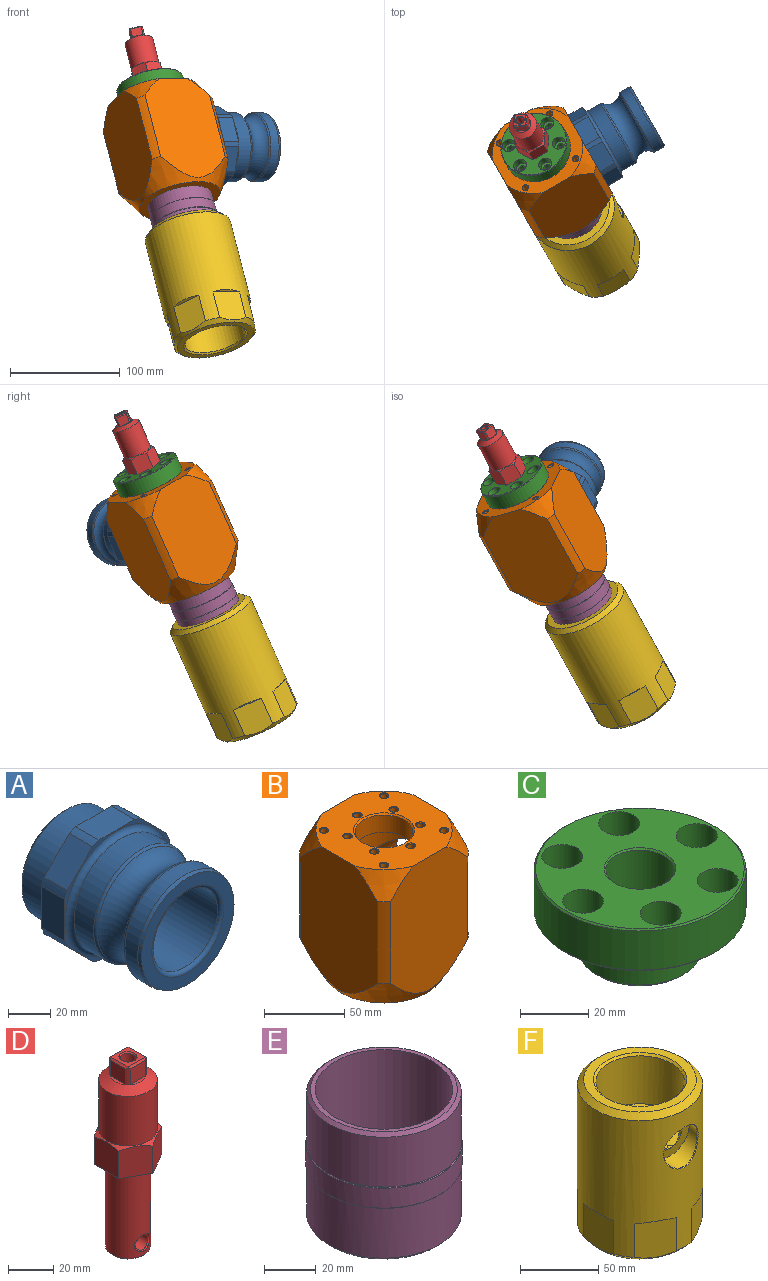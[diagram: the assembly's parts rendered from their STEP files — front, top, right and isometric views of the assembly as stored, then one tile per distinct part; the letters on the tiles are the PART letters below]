
ASSEMBLY  parts=6 mates=14
PART A: 42 faces, bbox 80.5x83x80.5 mm
  f0: plane 70x70mm, normal (0,-1,0), area 304.1mm2, adj f1,f2,f4,f5,f6,f7,f8,f9
  f1: cylinder r=37mm len=15.5mm, axis (0,-1,0), area 71.6mm2, adj f0,f3,f36,f37
  f2: cylinder r=37mm len=15.5mm, axis (0,-1,0), area 71.6mm2, adj f0,f3,f35,f37
  f3: plane 70x70mm, normal (0,1,0), area 622.2mm2, adj f1,f2,f4,f5,f6,f7,f8,f9
  f4: cylinder r=37mm len=15.5mm, axis (0,-1,0), area 71.6mm2, adj f0,f3,f30,f36
  f5: cylinder r=37mm len=15.5mm, axis (0,-1,0), area 71.6mm2, adj f0,f3,f34,f35
  f6: cylinder r=37mm len=15.5mm, axis (0,-1,0), area 71.6mm2, adj f0,f3,f33,f34
  f7: cylinder r=37mm len=15.5mm, axis (0,-1,0), area 71.6mm2, adj f0,f3,f32,f33
  f8: cylinder r=37mm len=15.5mm, axis (0,-1,0), area 71.6mm2, adj f0,f3,f31,f32
  f9: cylinder r=37mm len=15.5mm, axis (0,-1,0), area 71.6mm2, adj f0,f3,f30,f31
  f10: torus R=24mm, axis (0,-1,0), area 448.6mm2, adj f11,f29
  f11: plane 61.93x61.93mm, normal (0,-1,0), area 1202.5mm2, adj f10,f12
  f12: cone r=31.5mm half-angle=15deg, axis (0,1,0), area 406.3mm2, adj f11,f13
  f13: cylinder r=31.5mm len=63mm, axis (0,-1,0), area 1687.4mm2, adj f12,f14
  f14: torus R=29.5mm, axis (0,-1,0), area 367.6mm2, adj f13,f15
  f15: torus R=37.2mm, axis (0,-1,0), area 3592.5mm2, adj f14,f16
  f16: torus R=29.5mm, axis (0,-1,0), area 367.6mm2, adj f15,f17
  f17: cylinder r=31.5mm len=63mm, axis (0,-1,0), area 2578.1mm2, adj f16,f18
  f18: torus R=34.5mm, axis (0,-1,0), area 965mm2, adj f0,f17
  f19: cylinder r=33mm len=66mm, axis (0,-1,0), area 311mm2, adj f3,f41
  f20: plane 65x65mm, normal (0,1,0), area 395.8mm2, adj f40,f41
  f21: cylinder r=30mm len=60mm, axis (0,-1,0), area 282.7mm2, adj f22,f40
  f22: plane 60x60mm, normal (0,1,0), area 230.7mm2, adj f21,f38
  f23: cylinder r=28.25mm len=56.5mm, axis (0,-1,0), area 443.7mm2, adj f38,f39
  f24: plane 60x60mm, normal (0,-1,0), area 230.7mm2, adj f25,f39
  f25: cylinder r=30mm len=60mm, axis (0,-1,0), area 2733.2mm2, adj f24,f26
  f26: cone r=28mm half-angle=45deg, axis (0,-1,0), area 515.4mm2, adj f25,f27
  f27: plane 56x56mm, normal (0,1,0), area 653.5mm2, adj f26,f28
  f28: torus R=24mm, axis (0,-1,0), area 448.6mm2, adj f27,f29
  f29: cylinder r=22mm len=79mm, axis (0,-1,0), area 10920.2mm2, adj f10,f28
  f30: plane 16.97x16.97mm, normal (-0.71,0,0.71), area 372mm2, adj f0,f3,f4,f9
  f31: plane 24x15.5mm, normal (-1,0,0), area 372mm2, adj f0,f3,f8,f9
  f32: plane 16.97x16.97mm, normal (-0.71,0,-0.71), area 372mm2, adj f0,f3,f7,f8
  f33: plane 24x15.5mm, normal (0,0,-1), area 372mm2, adj f0,f3,f6,f7
  f34: plane 16.97x16.97mm, normal (0.71,0,-0.71), area 372mm2, adj f0,f3,f5,f6
  f35: plane 24x15.5mm, normal (1,0,0), area 372mm2, adj f0,f2,f3,f5
  f36: plane 24x15.5mm, normal (0,0,1), area 372mm2, adj f0,f1,f3,f4
  f37: plane 16.97x16.97mm, normal (0.71,0,0.71), area 372mm2, adj f0,f1,f2,f3
  f38: torus R=28.75mm, axis (0,-1,0), area 140.3mm2, adj f22,f23
  f39: torus R=28.75mm, axis (0,1,0), area 140.3mm2, adj f23,f24
  f40: torus R=30.5mm, axis (0,-1,0), area 148.9mm2, adj f20,f21
  f41: torus R=32.5mm, axis (0,-1,0), area 162mm2, adj f19,f20
PART B: 56 faces, bbox 105x105x105 mm
  f0: cylinder r=26mm len=63mm, axis (0,0,-1), area 6906.9mm2, adj f18,f19,f39,f40,f41
  f1: plane 80x80mm, normal (0,0,1), area 4065mm2, adj f4,f6,f8,f10,f11,f12,f13,f14
  f2: plane 76x76mm, normal (0,0,-1), area 1741.4mm2, adj f15,f46
  f3: cylinder r=52.5mm len=62.56mm, axis (0,0,-1), area 531.1mm2, adj f4,f10,f11,f15
  f4: plane 101.56x68.04mm, normal (1,0,0), area 3286.4mm2, adj f1,f3,f5,f11,f12,f15,f45
  f5: cylinder r=52.5mm len=62.56mm, axis (0,0,-1), area 531.1mm2, adj f4,f6,f12,f15
  f6: plane 101.56x68.04mm, normal (0,1,0), area 6081.5mm2, adj f1,f5,f7,f12,f13,f15
  f7: cylinder r=52.5mm len=62.56mm, axis (0,0,-1), area 531.1mm2, adj f6,f8,f13,f15
  f8: plane 101.56x68.04mm, normal (-1,0,0), area 6081.5mm2, adj f1,f7,f9,f13,f14,f15
  f9: cylinder r=52.5mm len=62.56mm, axis (0,0,-1), area 531.1mm2, adj f8,f10,f14,f15
  f10: plane 101.56x68.04mm, normal (0,-1,0), area 6081.5mm2, adj f1,f3,f9,f11,f14,f15
  f11: cone r=42.5mm half-angle=30deg, axis (0,0,-1), area 425.1mm2, adj f1,f3,f4,f10
  f12: cone r=42.5mm half-angle=30deg, axis (0,0,-1), area 425.1mm2, adj f1,f4,f5,f6
  f13: cone r=42.5mm half-angle=30deg, axis (0,0,-1), area 425.1mm2, adj f1,f6,f7,f8
  f14: cone r=42.5mm half-angle=30deg, axis (0,0,-1), area 425.1mm2, adj f1,f8,f9,f10
  f15: cone r=55mm half-angle=30deg, axis (0,0,1), area 3590.8mm2, adj f2,f3,f4,f5,f6,f7,f8,f9
  f16: cone r=19mm half-angle=45deg, axis (0,0,1), area 164.4mm2, adj f1,f17
  f17: cylinder r=18mm len=36mm, axis (0,0,-1), area 1492.1mm2, adj f16,f18
  f18: cone r=18mm half-angle=59deg, axis (0,0,-1), area 1290.1mm2, adj f0,f17
  f19: plane 56.66x56.66mm, normal (0,0,-1), area 397.3mm2, adj f0,f20
  f20: cylinder r=28.33mm len=56.66mm, axis (0,0,-1), area 3826.8mm2, adj f19,f46
  f21: cone r=3mm half-angle=46deg, axis (0,0,1), area 12mm2, adj f1,f22
  f22: cylinder r=2.5mm len=14.52mm, axis (0,0,1), area 228mm2, adj f21,f23
  f23: cone r=2.5mm half-angle=59deg, axis (0,0,1), area 22.9mm2, adj f22
  f24: cone r=3mm half-angle=46deg, axis (0,0,1), area 12mm2, adj f1,f25
  f25: cylinder r=2.5mm len=14.52mm, axis (0,0,1), area 228mm2, adj f24,f26
  f26: cone r=2.5mm half-angle=59deg, axis (0,0,1), area 22.9mm2, adj f25
  f27: cone r=3mm half-angle=46deg, axis (0,0,1), area 12mm2, adj f1,f28
  f28: cylinder r=2.5mm len=14.52mm, axis (0,0,1), area 228mm2, adj f27,f29
  f29: cone r=2.5mm half-angle=59deg, axis (0,0,1), area 22.9mm2, adj f28
  f30: cone r=3mm half-angle=46deg, axis (0,0,1), area 12mm2, adj f1,f31
  f31: cylinder r=2.5mm len=14.52mm, axis (0,0,1), area 228mm2, adj f30,f32
  f32: cone r=2.5mm half-angle=59deg, axis (0,0,1), area 22.9mm2, adj f31
  f33: cone r=3mm half-angle=46deg, axis (0,0,1), area 12mm2, adj f1,f34
  f34: cylinder r=2.5mm len=14.52mm, axis (0,0,1), area 228mm2, adj f33,f35
  f35: cone r=2.5mm half-angle=59deg, axis (0,0,1), area 22.9mm2, adj f34
  f36: cone r=3mm half-angle=46deg, axis (0,0,1), area 12mm2, adj f1,f37
  f37: cylinder r=2.5mm len=14.52mm, axis (0,0,1), area 228mm2, adj f36,f38
  f38: cone r=2.5mm half-angle=59deg, axis (0,0,1), area 22.9mm2, adj f37
  f39: plane 22.49x2.33mm, normal (1,0,0), area 35.2mm2, adj f0,f40
  f40: cylinder r=28.33mm len=56.66mm, axis (1,0,0), area 4362.6mm2, adj f0,f39,f41,f45
  f41: plane 22.49x2.33mm, normal (1,0,0), area 35.2mm2, adj f0,f40
  f42: cone r=3mm half-angle=46deg, axis (0,0,1), area 12mm2, adj f1,f43
  f43: cylinder r=2.5mm len=14.52mm, axis (0,0,1), area 228mm2, adj f42,f44
  f44: cone r=2.5mm half-angle=59deg, axis (0,0,1), area 22.9mm2, adj f43
  f45: cone r=28.33mm half-angle=45deg, axis (1,0,0), area 387.6mm2, adj f4,f40
  f46: cone r=28.33mm half-angle=45deg, axis (0,0,-1), area 387.6mm2, adj f2,f20
  f47: cone r=3mm half-angle=46deg, axis (0,0,1), area 12mm2, adj f1,f48
  f48: cylinder r=2.5mm len=14.52mm, axis (0,0,1), area 228mm2, adj f47,f49
  f49: cone r=2.5mm half-angle=59deg, axis (0,0,1), area 22.9mm2, adj f48
  f50: cone r=3mm half-angle=46deg, axis (0,0,1), area 12mm2, adj f1,f51
  f51: cylinder r=2.5mm len=14.52mm, axis (0,0,1), area 228mm2, adj f50,f52
  f52: cone r=2.5mm half-angle=59deg, axis (0,0,1), area 22.9mm2, adj f51
  f53: cone r=3mm half-angle=46deg, axis (0,0,1), area 12mm2, adj f1,f54
  f54: cylinder r=2.5mm len=14.52mm, axis (0,0,1), area 228mm2, adj f53,f55
  f55: cone r=2.5mm half-angle=59deg, axis (0,0,1), area 22.9mm2, adj f54
PART C: 37 faces, bbox 62x62x30 mm
  f0: cylinder r=17.98mm len=35.95mm, axis (0,0,-1), area 609.9mm2, adj f1,f18
  f1: plane 35.95x35.95mm, normal (0,0,-1), area 159.8mm2, adj f0,f2
  f2: cylinder r=16.5mm len=33mm, axis (0,0,-1), area 269.5mm2, adj f1,f3
  f3: plane 35.95x35.95mm, normal (0,0,1), area 159.8mm2, adj f2,f4
  f4: cylinder r=17.98mm len=35.95mm, axis (0,0,-1), area 677.6mm2, adj f3,f5
  f5: cone r=16.98mm half-angle=45deg, axis (0,0,1), area 155.3mm2, adj f4,f6
  f6: plane 33.95x33.95mm, normal (0,0,-1), area 558.9mm2, adj f5,f7
  f7: cone r=10mm half-angle=45deg, axis (0,0,-1), area 45.5mm2, adj f6,f8
  f8: cylinder r=10mm len=20mm, axis (0,0,-1), area 157.1mm2, adj f7,f9
  f9: plane 23x23mm, normal (0,0,1), area 101.3mm2, adj f8,f10
  f10: cylinder r=11.5mm len=23mm, axis (0,0,-1), area 187.9mm2, adj f9,f11
  f11: plane 23x23mm, normal (0,0,-1), area 101.3mm2, adj f10,f12
  f12: cylinder r=10mm len=23.9mm, axis (0,0,-1), area 1501.7mm2, adj f11,f13
  f13: cone r=10.5mm half-angle=45deg, axis (0,0,1), area 45.5mm2, adj f12,f14
  f14: plane 61x61mm, normal (0,0,1), area 1897.5mm2, adj f13,f15,f19,f22,f25,f28,f31,f34
  f15: cone r=31mm half-angle=45deg, axis (0,0,-1), area 136.6mm2, adj f14,f16
  f16: cylinder r=31mm len=62mm, axis (0,0,-1), area 2726.9mm2, adj f15,f17
  f17: cone r=30.5mm half-angle=45deg, axis (0,0,1), area 136.6mm2, adj f16,f18
  f18: plane 61x61mm, normal (0,0,-1), area 1676.5mm2, adj f0,f17,f21,f24,f27,f30,f33,f36
  f19: cylinder r=6mm len=12mm, axis (0,0,1), area 339.3mm2, adj f14,f20
  f20: plane 12x12mm, normal (0,0,1), area 74.6mm2, adj f19,f21
  f21: cylinder r=3.5mm len=7mm, axis (0,0,1), area 131.9mm2, adj f18,f20
  f22: cylinder r=6mm len=12mm, axis (0,0,1), area 339.3mm2, adj f14,f23
  f23: plane 12x12mm, normal (0,0,1), area 74.6mm2, adj f22,f24
  f24: cylinder r=3.5mm len=7mm, axis (0,0,1), area 131.9mm2, adj f18,f23
  f25: cylinder r=6mm len=12mm, axis (0,0,1), area 339.3mm2, adj f14,f26
  f26: plane 12x12mm, normal (0,0,1), area 74.6mm2, adj f25,f27
  f27: cylinder r=3.5mm len=7mm, axis (0,0,1), area 131.9mm2, adj f18,f26
  f28: cylinder r=6mm len=12mm, axis (0,0,1), area 339.3mm2, adj f14,f29
  f29: plane 12x12mm, normal (0,0,1), area 74.6mm2, adj f28,f30
  f30: cylinder r=3.5mm len=7mm, axis (0,0,1), area 131.9mm2, adj f18,f29
  f31: cylinder r=6mm len=12mm, axis (0,0,1), area 339.3mm2, adj f14,f32
  f32: plane 12x12mm, normal (0,0,1), area 74.6mm2, adj f31,f33
  f33: cylinder r=3.5mm len=7mm, axis (0,0,1), area 131.9mm2, adj f18,f32
  f34: cylinder r=6mm len=12mm, axis (0,0,1), area 339.3mm2, adj f14,f35
  f35: plane 12x12mm, normal (0,0,1), area 74.6mm2, adj f34,f36
  f36: cylinder r=3.5mm len=7mm, axis (0,0,1), area 131.9mm2, adj f18,f35
PART D: 36 faces, bbox 31.2x31.2x103.5 mm
  f0: plane 31.18x27mm, normal (0,0,-1), area 317.2mm2, adj f4,f5,f6,f7,f8,f9,f30
  f1: plane 9.72x1.65mm, normal (0,0,1), area 10.9mm2, adj f12,f21
  f2: plane 9.73x1.65mm, normal (0,0,1), area 10.9mm2, adj f12,f19
  f3: plane 9.74x1.65mm, normal (0,0,1), area 11mm2, adj f12,f17
  f4: plane 16x13.5mm, normal (0.5,0.87,0), area 243mm2, adj f0,f5,f9,f10
  f5: plane 16x13.5mm, normal (-0.5,0.87,0), area 243mm2, adj f0,f4,f6,f10
  f6: plane 16x15.6mm, normal (-1,0,0), area 243mm2, adj f0,f5,f7,f10
  f7: plane 16x13.5mm, normal (-0.5,-0.87,0), area 243mm2, adj f0,f6,f8,f10
  f8: plane 16x13.5mm, normal (0.5,-0.87,0), area 243mm2, adj f0,f7,f9,f10
  f9: plane 16x15.6mm, normal (1,0,0), area 243mm2, adj f0,f4,f8,f10
  f10: cone r=18.5mm half-angle=60deg, axis (0,0,-1), area 115.9mm2, adj f4,f5,f6,f7,f8,f9,f13
  f11: plane 9.73x1.65mm, normal (0,0,1), area 10.9mm2, adj f12,f15
  f12: cone r=13mm half-angle=60deg, axis (0,0,-1), area 380.9mm2, adj f1,f2,f3,f11,f13,f14,f16,f18
  f13: cylinder r=13mm len=26.82mm, axis (0,0,-1), area 2191.1mm2, adj f10,f12
  f14: cylinder r=8mm len=9.19mm, axis (0,0,-1), area 18.7mm2, adj f12,f15,f21,f24,f26
  f15: plane 9.73x8.5mm, normal (1,0,0), area 82.7mm2, adj f11,f14,f16,f24
  f16: cylinder r=8mm len=9.19mm, axis (0,0,-1), area 18.6mm2, adj f12,f15,f17,f24,f25
  f17: plane 9.74x8.5mm, normal (0,1,0), area 82.8mm2, adj f3,f16,f18,f25
  f18: cylinder r=8mm len=9.19mm, axis (0,0,-1), area 18.6mm2, adj f12,f17,f19,f23,f25
  f19: plane 9.73x8.5mm, normal (-1,0,0), area 82.7mm2, adj f2,f18,f20,f23
  f20: cylinder r=8mm len=9.19mm, axis (0,0,-1), area 18.7mm2, adj f12,f19,f21,f23,f26
  f21: plane 9.72x8.5mm, normal (0,-1,0), area 82.7mm2, adj f1,f14,f20,f26
  f22: plane 10.7x10.7mm, normal (0,0,1), area 64.2mm2, adj f23,f24,f25,f26,f27
  f23: plane 11.34x1.03mm, normal (-0.71,0,0.71), area 15.1mm2, adj f18,f19,f20,f22,f25,f26
  f24: plane 11.34x1.03mm, normal (0.71,0,0.71), area 15.1mm2, adj f14,f15,f16,f22,f25,f26
  f25: plane 11.34x1.03mm, normal (0,0.71,0.71), area 15.1mm2, adj f16,f17,f18,f22,f23,f24
  f26: plane 11.34x1.03mm, normal (0,-0.71,0.71), area 15.1mm2, adj f14,f20,f21,f22,f23,f24
  f27: cone r=4mm half-angle=46deg, axis (0,0,1), area 19.4mm2, adj f22,f28
  f28: cylinder r=3.4mm len=15.17mm, axis (0,0,1), area 324.1mm2, adj f27,f29
  f29: cone r=3.4mm half-angle=59deg, axis (0,0,1), area 42.4mm2, adj f28
  f30: cylinder r=10mm len=47mm, axis (0,0,1), area 2825.7mm2, adj f0,f32,f34,f35
  f31: plane 18x18mm, normal (0,0,-1), area 254.5mm2, adj f32
  f32: cone r=9mm half-angle=45deg, axis (0,0,1), area 84.4mm2, adj f30,f31
  f33: cylinder r=4mm len=18.17mm, axis (0,-1,0), area 442.3mm2, adj f34,f35
  f34: bspline ~9.47x8.99mm, area 21.6mm2, adj f30,f33
  f35: bspline ~8.69x8.36mm, area 11.9mm2, adj f30,f33
PART E: 12 faces, bbox 60.3x60.3x60 mm
  f0: cylinder r=30.15mm len=60.3mm, axis (0,0,-1), area 1780.7mm2, adj f10,f11
  f1: plane 56.6x56.6mm, normal (0,0,-1), area 309.9mm2, adj f3,f9
  f2: plane 56.6x56.6mm, normal (0,0,1), area 309.9mm2, adj f3,f8
  f3: cylinder r=26.5mm len=60mm, axis (0,0,-1), area 9990.3mm2, adj f1,f2
  f4: plane 59.7x59.7mm, normal (0,0,1), area 9.4mm2, adj f5,f10
  f5: cylinder r=29.8mm len=59.6mm, axis (0,0,1), area 4400.1mm2, adj f4,f8
  f6: plane 59.7x59.7mm, normal (0,0,-1), area 9.4mm2, adj f7,f11
  f7: cylinder r=29.8mm len=59.6mm, axis (0,0,-1), area 4400.1mm2, adj f6,f9
  f8: cone r=28.3mm half-angle=45deg, axis (0,0,-1), area 387.2mm2, adj f2,f5
  f9: cone r=28.3mm half-angle=45deg, axis (0,0,1), area 387.2mm2, adj f1,f7
  f10: cone r=29.85mm half-angle=45deg, axis (0,0,-1), area 80mm2, adj f0,f4
  f11: cone r=29.85mm half-angle=45deg, axis (0,0,1), area 80mm2, adj f0,f6
PART F: 46 faces, bbox 82.9x86.7x117.9 mm
  f0: cone r=29.8mm half-angle=45deg, axis (0,0,-1), area 387.2mm2, adj f1,f45
  f1: plane 72x72mm, normal (0,0,-1), area 1281.6mm2, adj f0,f2
  f2: cone r=40mm half-angle=45deg, axis (0,0,1), area 954.4mm2, adj f1,f3,f5,f7,f9,f11,f13,f15
  f3: plane 28.51x24.11mm, normal (-0.5,0.87,0), area 769.9mm2, adj f2,f4,f15
  f4: plane 27x16.81mm, normal (-0.25,0.43,-0.87), area 53.9mm2, adj f3,f15
  f5: plane 28.51x27.86mm, normal (-1,0,0), area 769.9mm2, adj f2,f6,f15
  f6: plane 30.73x5.39mm, normal (-0.5,0,-0.87), area 53.9mm2, adj f5,f15
  f7: plane 28.51x24.11mm, normal (-0.5,-0.87,0), area 769.9mm2, adj f2,f8,f15
  f8: plane 27x16.81mm, normal (-0.25,-0.43,-0.87), area 53.9mm2, adj f7,f15
  f9: plane 28.51x24.11mm, normal (0.5,-0.87,0), area 769.9mm2, adj f2,f10,f15
  f10: plane 27x16.81mm, normal (0.25,-0.43,-0.87), area 53.9mm2, adj f9,f15
  f11: plane 28.51x27.89mm, normal (1,0,0), area 769.9mm2, adj f2,f12,f15
  f12: plane 30.73x5.39mm, normal (0.5,0,-0.87), area 53.9mm2, adj f11,f15
  f13: plane 28.51x24.11mm, normal (0.5,0.87,0), area 769.9mm2, adj f2,f14,f15
  f14: plane 27x16.81mm, normal (0.25,0.43,-0.87), area 53.9mm2, adj f13,f15
  f15: cylinder r=40mm len=107mm, axis (0,0,-1), area 21671.7mm2, adj f2,f3,f4,f5,f6,f7,f8,f9
  f16: bspline ~31.26x31.23mm, area 63.7mm2, adj f15,f17
  f17: cylinder r=15.1mm len=31.68mm, axis (0,-0.99,-0.14), area 1207.6mm2, adj f16,f18
  f18: plane 30.21x29.92mm, normal (0,-0.99,-0.14), area 514.8mm2, adj f17,f19,f20,f23,f43
  f19: cylinder r=8mm len=16mm, axis (0,-0.99,-0.14), area 0mm2, adj f18,f20
  f20: cylinder r=28.3mm len=56.6mm, axis (0,0,-1), area 6464mm2, adj f18,f19,f21,f23
  f21: cone r=28.3mm half-angle=45deg, axis (0,0,1), area 387.2mm2, adj f20,f22
  f22: plane 72x72mm, normal (0,0,1), area 1281.6mm2, adj f21,f44
  f23: plane 56.6x56.35mm, normal (0,0,1), area 1148.9mm2, adj f18,f20,f24,f43
  f24: cone r=20.78mm half-angle=15deg, axis (0,0,1), area 397.6mm2, adj f23,f25
  f25: cylinder r=19.98mm len=39.95mm, axis (0,0,-1), area 2161.5mm2, adj f24,f26,f27,f32,f33,f34,f35,f36
  f26: cone r=8mm half-angle=59deg, axis (0,0,-1), area 127.8mm2, adj f25,f27
  f27: cylinder r=8mm len=30mm, axis (0,0,-1), area 1398.7mm2, adj f25,f26,f28,f42
  f28: plane 56.6x56.6mm, normal (0,0,-1), area 1123.4mm2, adj f27,f29,f33,f35,f37,f39,f41,f45
  f29: cone r=7.7mm half-angle=45deg, axis (0,0,-1), area 92.6mm2, adj f28,f30
  f30: cylinder r=6.2mm len=22mm, axis (0,0,-1), area 857mm2, adj f29,f31
  f31: cone r=6.2mm half-angle=45deg, axis (0,0,1), area 92.6mm2, adj f30,f42
  f32: cone r=8mm half-angle=59deg, axis (0,0,-1), area 127.8mm2, adj f25,f33
  f33: cylinder r=8mm len=30mm, axis (0,0,-1), area 1398.7mm2, adj f25,f28,f32,f42
  f34: cone r=8mm half-angle=59deg, axis (0,0,-1), area 127.8mm2, adj f25,f35
  f35: cylinder r=8mm len=30mm, axis (0,0,-1), area 1398.7mm2, adj f25,f28,f34,f42
  f36: cone r=8mm half-angle=59deg, axis (0,0,-1), area 127.8mm2, adj f25,f37
  f37: cylinder r=8mm len=30mm, axis (0,0,-1), area 1398.7mm2, adj f25,f28,f36,f42
  f38: cone r=8mm half-angle=59deg, axis (0,0,-1), area 127.8mm2, adj f25,f39
  f39: cylinder r=8mm len=30mm, axis (0,0,-1), area 1398.7mm2, adj f25,f28,f38,f42
  f40: cone r=8mm half-angle=59deg, axis (0,0,-1), area 127.8mm2, adj f25,f41
  f41: cylinder r=8mm len=30mm, axis (0,0,-1), area 1398.7mm2, adj f25,f28,f40,f42
  f42: plane 39.95x36.75mm, normal (0,0,1), area 517.9mm2, adj f25,f27,f31,f33,f35,f37,f39,f41
  f43: cylinder r=8mm len=4.97mm, axis (0,-0.99,-0.14), area 9.4mm2, adj f18,f23
  f44: cone r=36mm half-angle=45deg, axis (0,0,-1), area 1350.6mm2, adj f15,f22
  f45: cylinder r=28.3mm len=56.6mm, axis (0,0,-1), area 4178.6mm2, adj f0,f28
PLACE A rot(axis=(0.73,-0.42,0.53),145.7deg) t=(124.2,143.04,-184.46)mm
PLACE B rot(axis=(-0.66,-0.18,0.73),40.3deg) t=(119.45,111.28,-233.39)mm fixed
PLACE C rot(axis=(-0.44,0,0.9),65.3deg) t=(95.46,152.82,-139.99)mm
PLACE D rot(axis=(-0.87,-0.5,0),27.2deg) t=(92.04,158.75,-126.64)mm
PLACE E rot(axis=(-0.87,-0.5,0),27.2deg) t=(130.18,92.68,-275.2)mm
PLACE F rot(axis=(-0.23,0.13,0.96),121.8deg) t=(152.11,54.7,-360.6)mm
MATE planar E.f0 <-> B.f0  axis (-0.23,0.4,0.89) through (116.48,116.42,-221.83)mm
MATE cylindrical B.f27 <-> C.f28  axis (-0.23,0.4,0.89) through (86.49,127.66,-147.96)mm
MATE planar B.f4 <-> A.f1  axis (0.87,0.5,0) through (163.47,115.02,-195.51)mm
MATE cylindrical E.f0 <-> B.f0  axis (0.23,-0.4,-0.89) through (123.33,104.55,-248.51)mm
MATE cylindrical C.f0 <-> D.f10  axis (0.23,-0.4,-0.89) through (92.15,158.56,-127.09)mm
MATE planar F.f23 <-> E.f0  axis (-0.23,0.4,0.89) through (134.53,84.64,-292.99)mm
MATE parallel D.f5 <-> B.f6  axis (-0.44,0.77,-0.46) through (84.25,172.24,-125.87)mm
MATE cylindrical E.f0 <-> F.f0  axis (0.23,-0.4,-0.89) through (130.18,92.68,-275.2)mm
MATE planar C.f0 <-> B.f0  axis (0.23,-0.4,-0.89) through (95.46,152.82,-139.99)mm
MATE cylindrical A.f1 <-> B.f40  axis (0.87,0.5,0) through (196.08,184.54,-184.46)mm
MATE cylindrical C.f0 <-> B.f0  axis (-0.23,0.4,0.89) through (92.04,158.75,-126.64)mm
MATE parallel F.f7 <-> D.f15  axis (0.97,0.05,0.23) through (184.88,62.89,-337.65)mm
MATE planar D.f10 <-> C.f0  axis (0.23,-0.4,-0.89) through (92.04,158.75,-126.64)mm
MATE parallel A.f32 <-> B.f6  axis (-0.44,0.77,-0.46) through (132.67,183.88,-200.45)mm
